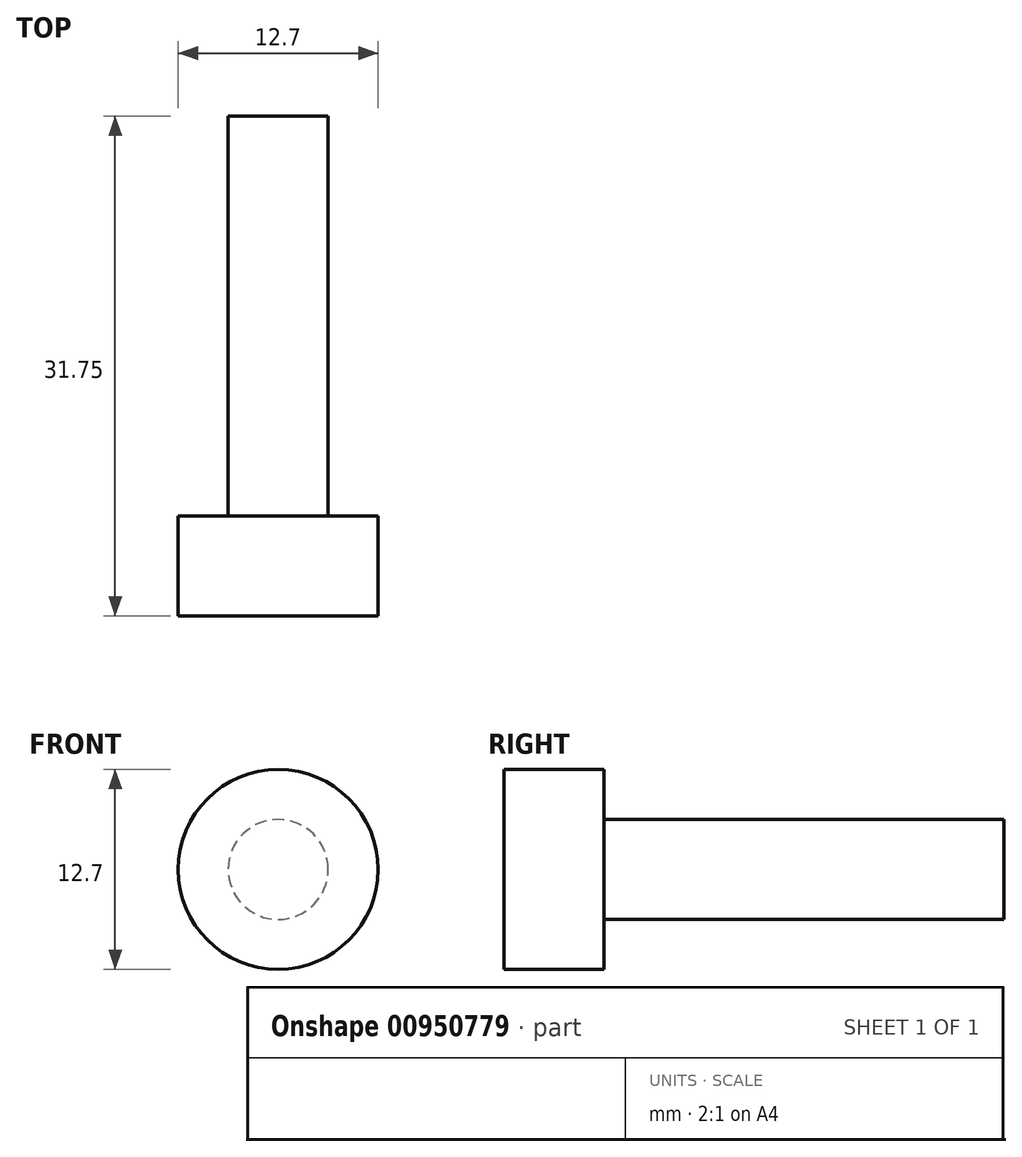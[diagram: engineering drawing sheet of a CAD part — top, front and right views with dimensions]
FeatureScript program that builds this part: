
annotation { "Feature Type Name" : "Feature", "Feature Type Description" : "" }
export const myFeature = defineFeature(function(context is Context, id is Id, definition is map)
    precondition{}
    {
        {
            var Q0;
            Q0=qCreatedBy(makeId("Front.planeOp"),FACE);
            var sketch = newSketch(context, id + "F0", { "sketchPlane" : qUnion([Q0])});
            skPoint(sketch, "E0", {"position": v(0, 0) * mm});
            skLineSegment(sketch, "E1", {"start": v(0, 0) * mm, "end": v(-3.18, 0) * mm});
            skCircle(sketch, "E2", {"center": v(0, 0) * mm, "radius": 3.18 * mm});
            skSolve(sketch);
        }
        {
            var Q0;
            Q0=makeQuery(id+"F0.imprint","IMPRINT",FACE,{"disambiguationData":[TD([[makeQuery(id+"F0.imprint","IMPRINT",EDGE,{"derivedFrom":sQuery(id+"F0.wireOp",EDGE,"E2")}),1.0]])]});
            extrude(context, id + "F1", {"entities" : qUnion([Q0]), "depth" : 25.4 * mm, "offsetDistance" : 25.4 * mm});
        }
        {
            var Q0;
            Q0=makeQuery(id+"F1.opExtrude","CAP_FACE",FACE,{"disambiguationData":[OSD([sQuery(id+"F0.wireOp",EDGE,"E2")])],"isStart":false});
            var sketch = newSketch(context, id + "F2", { "sketchPlane" : qUnion([Q0])});
            skLineSegment(sketch, "E3", {"start": v(0, 0) * mm, "end": v(-6.35, 0) * mm});
            skCircle(sketch, "E4", {"center": v(0, 0) * mm, "radius": 6.35 * mm});
            skSolve(sketch);
        }
        {
            var Q0;
            Q0=makeQuery(id+"F2.imprint","IMPRINT",FACE,{"disambiguationData":[TD([[makeQuery(id+"F2.imprint","IMPRINT",EDGE,{"derivedFrom":sQuery(id+"F2.wireOp",EDGE,"E4")}),1.0]])]});
            var Q1;
            Q1=makeQuery(id+"F2.imprint","IMPRINT",FACE,{"disambiguationData":[TD([[makeQuery(id+"F2.imprint","IMPRINT",EDGE,{"derivedFrom":makeQuery(id+"F1.opExtrude","CAP_EDGE",EDGE,{"disambiguationData":[OSD([sQuery(id+"F0.wireOp",EDGE,"E2")])],"isStart":false})}),1.0]])]});
            extrude(context, id + "F3", {"entities" : qUnion([Q0, Q1]), "operationType" : NewBodyOperationType.ADD, "depth" : 6.35 * mm, "offsetDistance" : 25.4 * mm});
        }
    });
